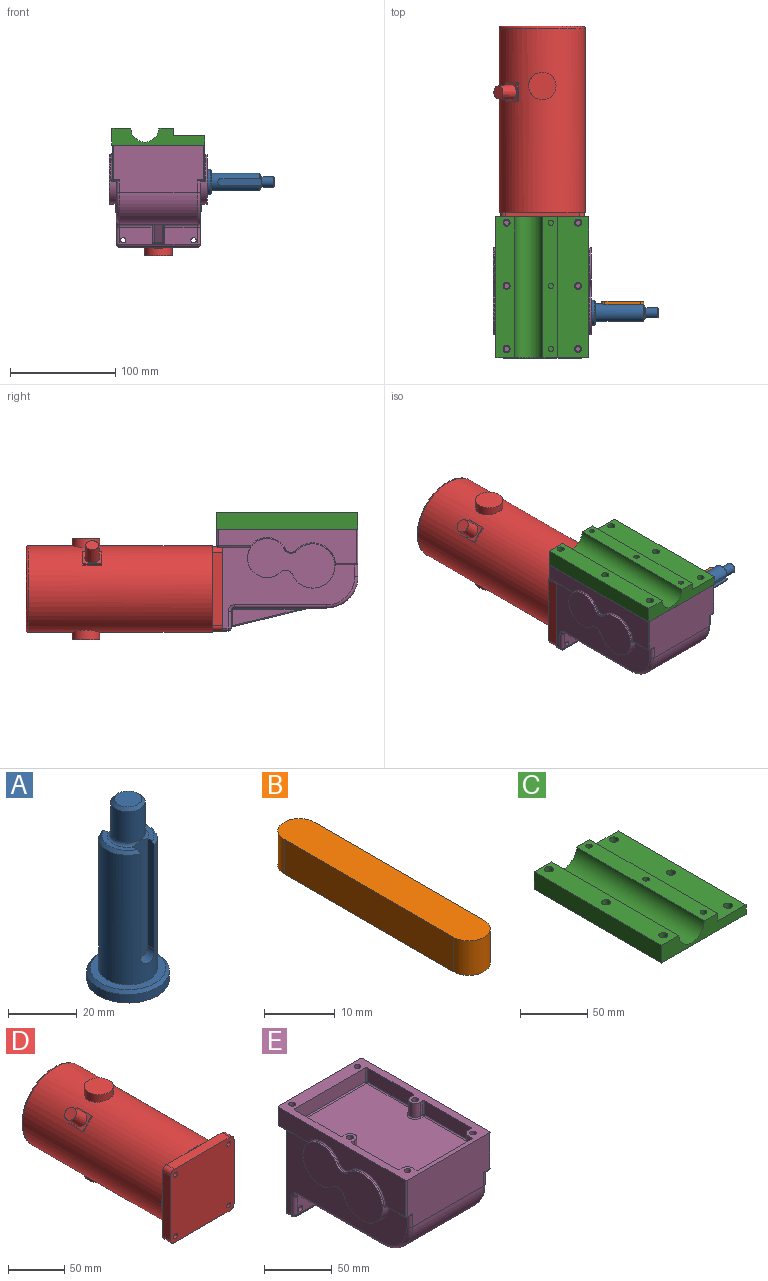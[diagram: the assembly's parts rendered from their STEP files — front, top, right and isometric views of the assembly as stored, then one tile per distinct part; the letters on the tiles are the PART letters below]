
ASSEMBLY  parts=5 mates=4
PART A: 21 faces, bbox 24x24x64 mm
  f0: plane 13.75x4.5mm, normal (0,0,1), area 22.7mm2, adj f10,f14,f18,f20
  f1: plane 13.75x4.5mm, normal (0,0,1), area 22.7mm2, adj f2,f12,f16,f20
  f2: cone r=7.5mm half-angle=45deg, axis (0,0,-1), area 26.8mm2, adj f1,f6,f12,f16
  f3: plane 24x24mm, normal (0,0,-1), area 452.4mm2, adj f4
  f4: cylinder r=12mm len=24mm, axis (0,0,1), area 226.2mm2, adj f3,f9
  f5: plane 22x22mm, normal (0,0,1), area 153.2mm2, adj f6,f9
  f6: cylinder r=8.5mm len=46mm, axis (0,0,1), area 1974.2mm2, adj f2,f5,f10,f12,f13,f14,f16,f17
  f7: cylinder r=4.98mm len=11mm, axis (0,0,1), area 344.2mm2, adj f11,f20
  f8: plane 7.96x7.96mm, normal (0,0,1), area 49.8mm2, adj f11
  f9: cone r=11mm half-angle=45deg, axis (0,0,-1), area 102.2mm2, adj f4,f5
  f10: cone r=7.5mm half-angle=45deg, axis (0,0,-1), area 26.8mm2, adj f0,f6,f14,f18
  f11: cone r=3.98mm half-angle=45deg, axis (0,0,-1), area 39.8mm2, adj f7,f8
  f12: plane 38.04x2.98mm, normal (1,0,0), area 111.7mm2, adj f1,f2,f6,f13,f15,f20
  f13: cylinder r=3mm len=6mm, axis (0,1,0), area 30.4mm2, adj f6,f12,f14,f15
  f14: plane 38.04x2.98mm, normal (-1,0,0), area 111.7mm2, adj f0,f6,f10,f13,f15,f20
  f15: plane 41.8x6mm, normal (0,-1,0), area 244.4mm2, adj f12,f13,f14,f20
  f16: plane 38.04x2.98mm, normal (1,0,0), area 111.7mm2, adj f1,f2,f6,f17,f19,f20
  f17: cylinder r=3mm len=6mm, axis (0,-1,0), area 30.4mm2, adj f6,f16,f18,f19
  f18: plane 38.04x2.98mm, normal (-1,0,0), area 111.7mm2, adj f0,f6,f10,f17,f19,f20
  f19: plane 41.8x6mm, normal (0,1,0), area 244.4mm2, adj f16,f17,f18,f20
  f20: torus R=5.98mm, axis (0,0,1), area 42.4mm2, adj f0,f1,f7,f12,f14,f15,f16,f18
PART B: 6 faces, bbox 6x40x6 mm
  f0: cylinder r=3mm len=6mm, axis (0,0,-1), area 56.5mm2, adj f1,f3,f4,f5
  f1: plane 34x6mm, normal (1,0,0), area 204mm2, adj f0,f2,f4,f5
  f2: cylinder r=3mm len=6mm, axis (0,0,-1), area 56.5mm2, adj f1,f3,f4,f5
  f3: plane 34x6mm, normal (-1,0,0), area 204mm2, adj f0,f2,f4,f5
  f4: plane 40x6mm, normal (0,0,1), area 232.3mm2, adj f0,f1,f2,f3
  f5: plane 40x6mm, normal (0,0,-1), area 232.3mm2, adj f0,f1,f2,f3
PART C: 22 faces, bbox 88.3x134x15.9 mm
  f0: plane 134x15.88mm, normal (-1,0,0), area 2127.2mm2, adj f1,f7,f8,f9
  f1: plane 134x88.25mm, normal (0,0,-1), area 11614mm2, adj f0,f2,f8,f9,f16,f17,f18,f19
  f2: plane 134x8.8mm, normal (1,0,0), area 1179.2mm2, adj f1,f3,f8,f9
  f3: plane 134x29.8mm, normal (0,0,1), area 3887.4mm2, adj f2,f4,f8,f9,f19,f20,f21
  f4: plane 134x7.08mm, normal (1,0,0), area 948mm2, adj f3,f5,f8,f9
  f5: plane 134x13.75mm, normal (0,0,1), area 1783.6mm2, adj f4,f6,f8,f9,f10,f12,f14
  f6: cylinder r=13.36mm len=134mm, axis (0,1,0), area 5520.3mm2, adj f5,f7,f8,f9
  f7: plane 134x18mm, normal (0,0,1), area 2306.2mm2, adj f0,f6,f8,f9,f16,f17,f18
  f8: plane 88.25x15.88mm, normal (0,-1,0), area 920.1mm2, adj f0,f1,f2,f3,f4,f5,f6,f7
  f9: plane 88.25x15.88mm, normal (0,1,0), area 920.1mm2, adj f0,f1,f2,f3,f4,f5,f6,f7
  f10: cylinder r=2.5mm len=7.08mm, axis (0,0,-1), area 111.1mm2, adj f5,f11
  f11: plane 5x5mm, normal (0,0,1), area 19.6mm2, adj f10
  f12: cylinder r=2.5mm len=7.08mm, axis (0,0,-1), area 111.1mm2, adj f5,f13
  f13: plane 5x5mm, normal (0,0,1), area 19.6mm2, adj f12
  f14: cylinder r=2.5mm len=7.08mm, axis (0,0,-1), area 111.1mm2, adj f5,f15
  f15: plane 5x5mm, normal (0,0,1), area 19.6mm2, adj f14
  f16: cylinder r=3.35mm len=15.88mm, axis (0,0,1), area 334.1mm2, adj f1,f7
  f17: cylinder r=3.35mm len=15.88mm, axis (0,0,1), area 334.1mm2, adj f1,f7
  f18: cylinder r=3.35mm len=15.88mm, axis (0,0,1), area 334.1mm2, adj f1,f7
  f19: cylinder r=3.35mm len=8.8mm, axis (0,0,1), area 185.2mm2, adj f1,f3
  f20: cylinder r=3.35mm len=8.8mm, axis (0,0,1), area 185.2mm2, adj f1,f3
  f21: cylinder r=3.35mm len=8.8mm, axis (0,0,1), area 185.2mm2, adj f1,f3
PART D: 35 faces, bbox 90.4x187x96 mm
  f0: cylinder r=41mm len=175mm, axis (0,-1,0), area 43717.7mm2, adj f1,f2,f3,f12,f14,f15,f16,f18
  f1: plane 31x31mm, normal (0,1,0), area 266.8mm2, adj f0,f4,f7,f11,f33
  f2: plane 31x31mm, normal (0,1,0), area 266.8mm2, adj f0,f6,f8,f11,f32
  f3: plane 31x31mm, normal (0,1,0), area 266.8mm2, adj f0,f5,f6,f9,f31
  f4: plane 70x10mm, normal (-1,0,0), area 700mm2, adj f1,f12,f13,f16,f30,f33
  f5: plane 70x10mm, normal (0,0,-1), area 700mm2, adj f3,f12,f13,f18,f30,f31
  f6: plane 70x10mm, normal (1,0,0), area 700mm2, adj f2,f3,f13,f15,f31,f32
  f7: cylinder r=2.5mm len=10mm, axis (0,-1,0), area 157.1mm2, adj f1,f13
  f8: cylinder r=2.5mm len=10mm, axis (0,-1,0), area 157.1mm2, adj f2,f13
  f9: cylinder r=2.5mm len=10mm, axis (0,-1,0), area 157.1mm2, adj f3,f13
  f10: cylinder r=2.5mm len=10mm, axis (0,-1,0), area 157.1mm2, adj f12,f13
  f11: plane 70x10mm, normal (0,0,1), area 700mm2, adj f1,f2,f13,f14,f32,f33
  f12: plane 31x31mm, normal (0,1,0), area 266.8mm2, adj f0,f4,f5,f10,f30
  f13: plane 80x80mm, normal (0,-1,0), area 6300mm2, adj f4,f5,f6,f7,f8,f9,f10,f11
  f14: plane 18x1mm, normal (0,-1,0), area 12mm2, adj f0,f11
  f15: plane 18x1mm, normal (0,-1,0), area 12mm2, adj f0,f6
  f16: plane 18x1mm, normal (0,-1,0), area 12mm2, adj f0,f4
  f17: plane 78x78mm, normal (0,1,0), area 4778.4mm2, adj f34
  f18: plane 18x1mm, normal (0,-1,0), area 12mm2, adj f0,f5
  f19: plane 26x26mm, normal (0,0,1), area 530.9mm2, adj f20
  f20: cylinder r=13mm len=26mm, axis (0,0,-1), area 657.5mm2, adj f0,f19
  f21: cylinder r=13mm len=26mm, axis (0,0,-1), area 657.6mm2, adj f0,f22
  f22: plane 26x26mm, normal (0,0,-1), area 530.9mm2, adj f21
  f23: plane 18x1.26mm, normal (0.71,0,0.71), area 32.2mm2, adj f0,f25,f26,f27
  f24: plane 18x1.26mm, normal (-0.71,0,-0.71), area 32.2mm2, adj f0,f25,f26,f27
  f25: plane 12.58x12.58mm, normal (0,1,0), area 20.2mm2, adj f0,f23,f24,f27
  f26: plane 12.58x12.58mm, normal (0,-1,0), area 20.2mm2, adj f0,f23,f24,f27
  f27: plane 18x11.31mm, normal (-0.71,0,0.71), area 134.1mm2, adj f23,f24,f25,f26,f28
  f28: cone r=7mm half-angle=3deg, axis (0.71,0,-0.71), area 701.1mm2, adj f27,f29
  f29: plane 12.22x8.64mm, normal (-0.71,0,0.71), area 117.2mm2, adj f28
  f30: cylinder r=5mm len=10mm, axis (0,-1,0), area 78.5mm2, adj f4,f5,f12,f13
  f31: cylinder r=5mm len=10mm, axis (0,1,0), area 78.5mm2, adj f3,f5,f6,f13
  f32: cylinder r=5mm len=10mm, axis (0,-1,0), area 78.5mm2, adj f2,f6,f11,f13
  f33: cylinder r=5mm len=10mm, axis (0,1,0), area 78.5mm2, adj f1,f4,f11,f13
  f34: torus R=39mm, axis (0,1,0), area 795mm2, adj f0,f17
PART E: 163 faces, bbox 93x136.5x97 mm
  f0: cylinder r=3mm len=31mm, axis (1,0,0), area 146.1mm2, adj f3,f10,f45,f150
  f1: plane 134x88mm, normal (0,0,1), area 2921.3mm2, adj f2,f24,f25,f26,f48,f57,f64,f69
  f2: plane 86x45mm, normal (0,-1,0), area 3726mm2, adj f1,f31,f32,f34,f48,f49,f56,f57
  f3: plane 87.5x74mm, normal (0,0,-1), area 5616.9mm2, adj f0,f31,f35,f41,f42,f149,f151,f154
  f4: plane 80x80mm, normal (0,1,0), area 6317.6mm2, adj f5,f6,f7,f8,f9,f11,f13,f23
  f5: plane 125.5x77mm, normal (1,0,0), area 4068.3mm2, adj f4,f19,f20,f21,f22,f23,f32,f33
  f6: plane 125.5x77mm, normal (-1,0,0), area 4068.3mm2, adj f4,f15,f16,f17,f18,f23,f34,f38
  f7: plane 74x5mm, normal (0,0,-1), area 370mm2, adj f4,f37,f43,f44
  f8: cylinder r=2.5mm len=8mm, axis (0,1,0), area 125.7mm2, adj f4,f10
  f9: cylinder r=2.5mm len=8mm, axis (0,1,0), area 125.7mm2, adj f4,f10
  f10: plane 74x16mm, normal (0,-1,0), area 957mm2, adj f0,f8,f9,f36,f42,f43,f47,f152
  f11: cylinder r=2.5mm len=6mm, axis (0,1,0), area 94.2mm2, adj f4,f12
  f12: plane 5x5mm, normal (0,1,0), area 19.6mm2, adj f11
  f13: cylinder r=2.5mm len=6mm, axis (0,1,0), area 94.2mm2, adj f4,f14
  f14: plane 5x5mm, normal (0,1,0), area 19.6mm2, adj f13
  f15: plane 20x3.76mm, normal (0,0,-1), area 60.5mm2, adj f6,f34,f49,f51,f52
  f16: cylinder r=21mm len=42mm, axis (-1,0,0), area 449.8mm2, adj f6,f17,f27,f28,f52,f53,f54
  f17: cylinder r=7.11mm len=11.42mm, axis (-1,0,0), area 88.9mm2, adj f6,f16,f18,f27
  f18: cylinder r=18.5mm len=37mm, axis (-1,0,0), area 402.3mm2, adj f6,f17,f27,f28,f58,f59,f61
  f19: plane 20x3.76mm, normal (0,0,-1), area 60.5mm2, adj f5,f32,f56,f62,f63
  f20: cylinder r=21mm len=42mm, axis (-1,0,0), area 449.8mm2, adj f5,f21,f29,f30,f62,f66,f68
  f21: cylinder r=7.11mm len=11.42mm, axis (-1,0,0), area 88.9mm2, adj f5,f20,f22,f30
  f22: cylinder r=18.5mm len=37mm, axis (-1,0,0), area 402.3mm2, adj f5,f21,f29,f30,f73,f75,f76
  f23: plane 86x29.51mm, normal (0,0,-1), area 537.1mm2, adj f4,f5,f6,f59,f65,f70,f74,f76
  f24: plane 86x16mm, normal (0,1,0), area 1376mm2, adj f1,f64,f69,f70
  f25: plane 132x33mm, normal (1,0,0), area 2354mm2, adj f1,f57,f63,f68,f69,f71,f73,f74
  f26: plane 132x33mm, normal (-1,0,0), area 2354mm2, adj f1,f48,f51,f54,f55,f58,f64,f65
  f27: plane 82.96x47mm, normal (-1,0,0), area 2565.2mm2, adj f16,f17,f18,f28
  f28: cylinder r=7.11mm len=11.55mm, axis (-1,0,0), area 20.5mm2, adj f16,f18,f27,f55
  f29: cylinder r=7.11mm len=11.55mm, axis (-1,0,0), area 20.5mm2, adj f20,f22,f30,f71
  f30: plane 82.96x47mm, normal (1,0,0), area 2565.2mm2, adj f20,f21,f22,f29
  f31: cylinder r=30mm len=74mm, axis (1,0,0), area 3487.2mm2, adj f2,f3,f33,f38
  f32: cylinder r=3mm len=12mm, axis (0,0,1), area 53.1mm2, adj f2,f5,f19,f33,f56
  f33: torus R=27mm, axis (1,0,0), area 214mm2, adj f5,f31,f32,f35
  f34: cylinder r=3mm len=12mm, axis (0,0,-1), area 53.1mm2, adj f2,f6,f15,f38,f49
  f35: cylinder r=3mm len=87.5mm, axis (0,-1,0), area 412.3mm2, adj f3,f5,f33,f39
  f36: cylinder r=3mm len=16mm, axis (0,0,-1), area 75.4mm2, adj f5,f10,f39,f40
  f37: cylinder r=3mm len=5mm, axis (0,-1,0), area 23.6mm2, adj f4,f5,f7,f40
  f38: torus R=27mm, axis (1,0,0), area 214mm2, adj f6,f31,f34,f41
  f39: torus R=6mm, axis (1,0,0), area 30.3mm2, adj f5,f35,f36,f42
  f40: sphere r=3mm, area 14.1mm2, adj f36,f37,f43
  f41: cylinder r=3mm len=87.5mm, axis (0,1,0), area 412.3mm2, adj f3,f6,f38,f45
  f42: cylinder r=3mm len=31mm, axis (1,0,0), area 146.1mm2, adj f3,f10,f39,f160
  f43: cylinder r=3mm len=74mm, axis (-1,0,0), area 348.7mm2, adj f7,f10,f40,f46
  f44: cylinder r=3mm len=5mm, axis (0,1,0), area 23.6mm2, adj f4,f6,f7,f46
  f45: torus R=6mm, axis (1,0,0), area 30.3mm2, adj f0,f6,f41,f47
  f46: sphere r=3mm, area 14.1mm2, adj f43,f44,f47
  f47: cylinder r=3mm len=16mm, axis (0,0,1), area 75.4mm2, adj f6,f10,f45,f46
  f48: cylinder r=1mm len=33mm, axis (0,0,-1), area 51.8mm2, adj f1,f2,f26,f50
  f49: cylinder r=1mm len=6mm, axis (-1,0,0), area 7.7mm2, adj f2,f15,f34,f50
  f50: sphere r=1mm, area 1.6mm2, adj f48,f49,f51
  f51: cylinder r=1mm len=20.09mm, axis (0,1,0), area 31.5mm2, adj f15,f26,f50,f53
  f52: cylinder r=1mm len=3mm, axis (-1,0,0), area 4.7mm2, adj f6,f15,f16,f53
  f53: bspline ~2.45x2.23mm, area 3.3mm2, adj f16,f51,f52,f54
  f54: torus R=22mm, axis (1,0,0), area 77.3mm2, adj f16,f26,f53,f55
  f55: torus R=6.11mm, axis (1,0,0), area 20.4mm2, adj f26,f28,f54,f58
  f56: cylinder r=1mm len=6mm, axis (-1,0,0), area 7.7mm2, adj f2,f19,f32,f60
  f57: cylinder r=1mm len=33mm, axis (0,0,1), area 51.8mm2, adj f1,f2,f25,f60
  f58: torus R=19.5mm, axis (1,0,0), area 60.5mm2, adj f18,f26,f55,f61
  f59: cylinder r=1mm len=3mm, axis (-1,0,0), area 6.2mm2, adj f6,f18,f23,f61
  f60: sphere r=1mm, area 1.6mm2, adj f56,f57,f63
  f61: bspline ~2.77x2.49mm, area 4.3mm2, adj f18,f58,f59,f65
  f62: cylinder r=1mm len=3mm, axis (-1,0,0), area 4.7mm2, adj f5,f19,f20,f66
  f63: cylinder r=1mm len=20.09mm, axis (0,-1,0), area 31.5mm2, adj f19,f25,f60,f66
  f64: cylinder r=1mm len=16mm, axis (0,0,1), area 25.1mm2, adj f1,f24,f26,f67
  f65: cylinder r=1mm len=30.79mm, axis (0,1,0), area 47.1mm2, adj f23,f26,f61,f67
  f66: bspline ~2.34x2.34mm, area 3.3mm2, adj f20,f62,f63,f68
  f67: sphere r=1mm, area 1.6mm2, adj f64,f65,f70
  f68: torus R=22mm, axis (1,0,0), area 77.3mm2, adj f20,f25,f66,f71
  f69: cylinder r=1mm len=16mm, axis (0,0,-1), area 25.1mm2, adj f1,f24,f25,f72
  f70: cylinder r=1mm len=86mm, axis (-1,0,0), area 135.1mm2, adj f23,f24,f67,f72
  f71: torus R=6.11mm, axis (1,0,0), area 20.4mm2, adj f25,f29,f68,f73
  f72: sphere r=1mm, area 1.6mm2, adj f69,f70,f74
  f73: torus R=19.5mm, axis (1,0,0), area 60.5mm2, adj f22,f25,f71,f75
  f74: cylinder r=1mm len=30.79mm, axis (0,-1,0), area 47.1mm2, adj f23,f25,f72,f75
  f75: bspline ~2.7x2.4mm, area 4.3mm2, adj f22,f73,f74,f76
  f76: cylinder r=1mm len=3mm, axis (-1,0,0), area 6.2mm2, adj f5,f22,f23,f75
  f77: plane 56x12.5mm, normal (0,1,0), area 700mm2, adj f1,f139,f143,f145
  f78: plane 12.5x4mm, normal (-1,0,0), area 50mm2, adj f1,f79,f138,f139
  f79: cylinder r=5mm len=12.5mm, axis (0,0,1), area 98.2mm2, adj f1,f78,f80,f136
  f80: plane 12.5x3mm, normal (0,1,0), area 37.5mm2, adj f1,f79,f129,f134
  f81: plane 48x12.5mm, normal (-1,0,0), area 600mm2, adj f1,f123,f128,f129
  f82: plane 12.5x3mm, normal (0,-1,0), area 37.5mm2, adj f1,f83,f122,f123
  f83: cylinder r=5mm len=12.5mm, axis (0,0,1), area 196.3mm2, adj f1,f82,f84,f120
  f84: plane 12.5x3mm, normal (0,1,0), area 37.5mm2, adj f1,f83,f113,f118
  f85: plane 47.5x12.5mm, normal (-1,0,0), area 593.8mm2, adj f1,f108,f112,f113
  f86: plane 74x12.5mm, normal (0,-1,0), area 925mm2, adj f1,f108,f110,f111
  f87: plane 47.5x12.5mm, normal (1,0,0), area 593.8mm2, adj f1,f110,f116,f117
  f88: plane 12.5x3mm, normal (0,1,0), area 37.5mm2, adj f1,f89,f116,f121
  f89: cylinder r=5mm len=12.5mm, axis (0,0,1), area 196.3mm2, adj f1,f88,f90,f124
  f90: plane 12.5x3mm, normal (0,-1,0), area 37.5mm2, adj f1,f89,f126,f127
  f91: plane 48x12.5mm, normal (1,0,0), area 600mm2, adj f1,f126,f132,f133
  f92: plane 12.5x3mm, normal (0,1,0), area 37.5mm2, adj f1,f93,f132,f137
  f93: cylinder r=5mm len=12.5mm, axis (0,0,1), area 98.2mm2, adj f1,f92,f94,f140
  f94: plane 12.5x4mm, normal (1,0,0), area 50mm2, adj f1,f93,f142,f145
  f95: plane 117.5x74mm, normal (0,0,1), area 8345.4mm2, adj f111,f112,f117,f118,f120,f121,f122,f124
  f96: cylinder r=2.5mm len=13.5mm, axis (0,0,1), area 212.1mm2, adj f1,f97
  f97: plane 5x5mm, normal (0,0,1), area 19.6mm2, adj f96
  f98: cylinder r=2.5mm len=13.5mm, axis (0,0,1), area 212.1mm2, adj f1,f99
  f99: plane 5x5mm, normal (0,0,1), area 19.6mm2, adj f98
  f100: cylinder r=2.5mm len=13.5mm, axis (0,0,1), area 212.1mm2, adj f1,f101
  f101: plane 5x5mm, normal (0,0,1), area 19.6mm2, adj f100
  f102: cylinder r=2.5mm len=13.5mm, axis (0,0,1), area 212.1mm2, adj f1,f103
  f103: plane 5x5mm, normal (0,0,1), area 19.6mm2, adj f102
  f104: cylinder r=2.5mm len=13.5mm, axis (0,0,1), area 212.1mm2, adj f1,f105
  f105: plane 5x5mm, normal (0,0,1), area 19.6mm2, adj f104
  f106: cylinder r=2.5mm len=13.5mm, axis (0,0,1), area 212.1mm2, adj f1,f107
  f107: plane 5x5mm, normal (0,0,1), area 19.6mm2, adj f106
  f108: cylinder r=1mm len=12.5mm, axis (0,0,1), area 19.6mm2, adj f1,f85,f86,f109
  f109: sphere r=1mm, area 1.6mm2, adj f108,f111,f112
  f110: cylinder r=1mm len=12.5mm, axis (0,0,-1), area 19.6mm2, adj f1,f86,f87,f114
  f111: cylinder r=1mm len=74mm, axis (-1,0,0), area 116.2mm2, adj f86,f95,f109,f114
  f112: cylinder r=1mm len=47.5mm, axis (0,1,0), area 74.6mm2, adj f85,f95,f109,f115
  f113: cylinder r=1mm len=12.5mm, axis (0,0,1), area 19.6mm2, adj f1,f84,f85,f115
  f114: sphere r=1mm, area 1.6mm2, adj f110,f111,f117
  f115: sphere r=1mm, area 1.6mm2, adj f112,f113,f118
  f116: cylinder r=1mm len=12.5mm, axis (0,0,1), area 19.6mm2, adj f1,f87,f88,f119
  f117: cylinder r=1mm len=47.5mm, axis (0,-1,0), area 74.6mm2, adj f87,f95,f114,f119
  f118: cylinder r=1mm len=3mm, axis (1,0,0), area 4.7mm2, adj f84,f95,f115,f120
  f119: sphere r=1mm, area 1.6mm2, adj f116,f117,f121
  f120: torus R=6mm, axis (0,0,1), area 26.5mm2, adj f83,f95,f118,f122
  f121: cylinder r=1mm len=3mm, axis (1,0,0), area 4.7mm2, adj f88,f95,f119,f124
  f122: cylinder r=1mm len=3mm, axis (-1,0,0), area 4.7mm2, adj f82,f95,f120,f125
  f123: cylinder r=1mm len=12.5mm, axis (0,0,-1), area 19.6mm2, adj f1,f81,f82,f125
  f124: torus R=6mm, axis (0,0,1), area 26.5mm2, adj f89,f95,f121,f127
  f125: sphere r=1mm, area 1.6mm2, adj f122,f123,f128
  f126: cylinder r=1mm len=12.5mm, axis (0,0,-1), area 19.6mm2, adj f1,f90,f91,f130
  f127: cylinder r=1mm len=3mm, axis (-1,0,0), area 4.7mm2, adj f90,f95,f124,f130
  f128: cylinder r=1mm len=48mm, axis (0,1,0), area 75.4mm2, adj f81,f95,f125,f131
  f129: cylinder r=1mm len=12.5mm, axis (0,0,1), area 19.6mm2, adj f1,f80,f81,f131
  f130: sphere r=1mm, area 1.6mm2, adj f126,f127,f133
  f131: sphere r=1mm, area 1.6mm2, adj f128,f129,f134
  f132: cylinder r=1mm len=12.5mm, axis (0,0,1), area 19.6mm2, adj f1,f91,f92,f135
  f133: cylinder r=1mm len=48mm, axis (0,-1,0), area 75.4mm2, adj f91,f95,f130,f135
  f134: cylinder r=1mm len=3mm, axis (1,0,0), area 4.7mm2, adj f80,f95,f131,f136
  f135: sphere r=1mm, area 1.6mm2, adj f132,f133,f137
  f136: torus R=6mm, axis (0,0,1), area 13.2mm2, adj f79,f95,f134,f138
  f137: cylinder r=1mm len=3mm, axis (1,0,0), area 4.7mm2, adj f92,f95,f135,f140
  f138: cylinder r=1mm len=4mm, axis (0,1,0), area 6.3mm2, adj f78,f95,f136,f141
  f139: cylinder r=1mm len=12.5mm, axis (0,0,-1), area 19.6mm2, adj f1,f77,f78,f141
  f140: torus R=6mm, axis (0,0,1), area 13.2mm2, adj f93,f95,f137,f142
  f141: sphere r=1mm, area 1.6mm2, adj f138,f139,f143
  f142: cylinder r=1mm len=4mm, axis (0,-1,0), area 6.3mm2, adj f94,f95,f140,f144
  f143: cylinder r=1mm len=56mm, axis (1,0,0), area 88mm2, adj f77,f95,f141,f144
  f144: sphere r=1mm, area 1.6mm2, adj f142,f143,f145
  f145: cylinder r=1mm len=12.5mm, axis (0,0,1), area 19.6mm2, adj f1,f77,f94,f144
  f146: plane 65.55x15.73mm, normal (1,0,0), area 514.7mm2, adj f157,f159,f160,f162
  f147: plane 65.55x15.73mm, normal (-1,0,0), area 514.7mm2, adj f149,f150,f152,f153
  f148: plane 74.12x17.79mm, normal (0,-0.23,-0.97), area 609.8mm2, adj f153,f154,f158,f159
  f149: cylinder r=1mm len=63.55mm, axis (0,1,0), area 99.8mm2, adj f3,f147,f150,f151
  f150: torus R=2mm, axis (1,0,0), area 6.5mm2, adj f0,f147,f149,f152
  f151: bspline ~8.57x2mm, area 8.8mm2, adj f3,f149,f153,f154
  f152: cylinder r=1mm len=13.73mm, axis (0,0,-1), area 21.6mm2, adj f10,f147,f150,f155
  f153: cylinder r=1mm len=74.35mm, axis (0,0.97,-0.23), area 114.6mm2, adj f147,f148,f151,f155
  f154: cylinder r=1mm len=8mm, axis (1,0,0), area 1.9mm2, adj f3,f148,f151,f156
  f155: bspline ~2.14x2.06mm, area 3.2mm2, adj f10,f152,f153,f158
  f156: bspline ~8.57x2mm, area 8.8mm2, adj f3,f154,f157,f159
  f157: cylinder r=1mm len=63.55mm, axis (0,-1,0), area 99.8mm2, adj f3,f146,f156,f160
  f158: cylinder r=1mm len=8mm, axis (1,0,0), area 10.7mm2, adj f10,f148,f155,f161
  f159: cylinder r=1mm len=74.35mm, axis (0,-0.97,0.23), area 114.6mm2, adj f146,f148,f156,f161
  f160: torus R=2mm, axis (1,0,0), area 6.5mm2, adj f42,f146,f157,f162
  f161: bspline ~2.41x2.35mm, area 3.2mm2, adj f10,f158,f159,f162
  f162: cylinder r=1mm len=13.73mm, axis (0,0,1), area 21.6mm2, adj f10,f146,f160,f161
PLACE A rot(axis=(0,1,0),90deg) t=(46.5,-85.5,22)mm
PLACE B rot(axis=(-0.58,-0.58,-0.58),120deg) t=(76.5,-80.5,22)mm
PLACE C at identity
PLACE D t=(0,0,0.02)mm
PLACE E at identity fixed
MATE fastened B.f0 <-> A.f13  axis (0,-1,0) through (59.5,-80.5,22)mm
MATE revolute A.f9 <-> E.f16  axis (-1,0,0) through (46.5,-85.5,22)mm
MATE fastened C.f20 <-> E.f79  axis (0,0,-1) through (34,-120,57)mm
MATE fastened D.f0 <-> E.f4  axis (0,-1,0) through (0,0,0.02)mm
